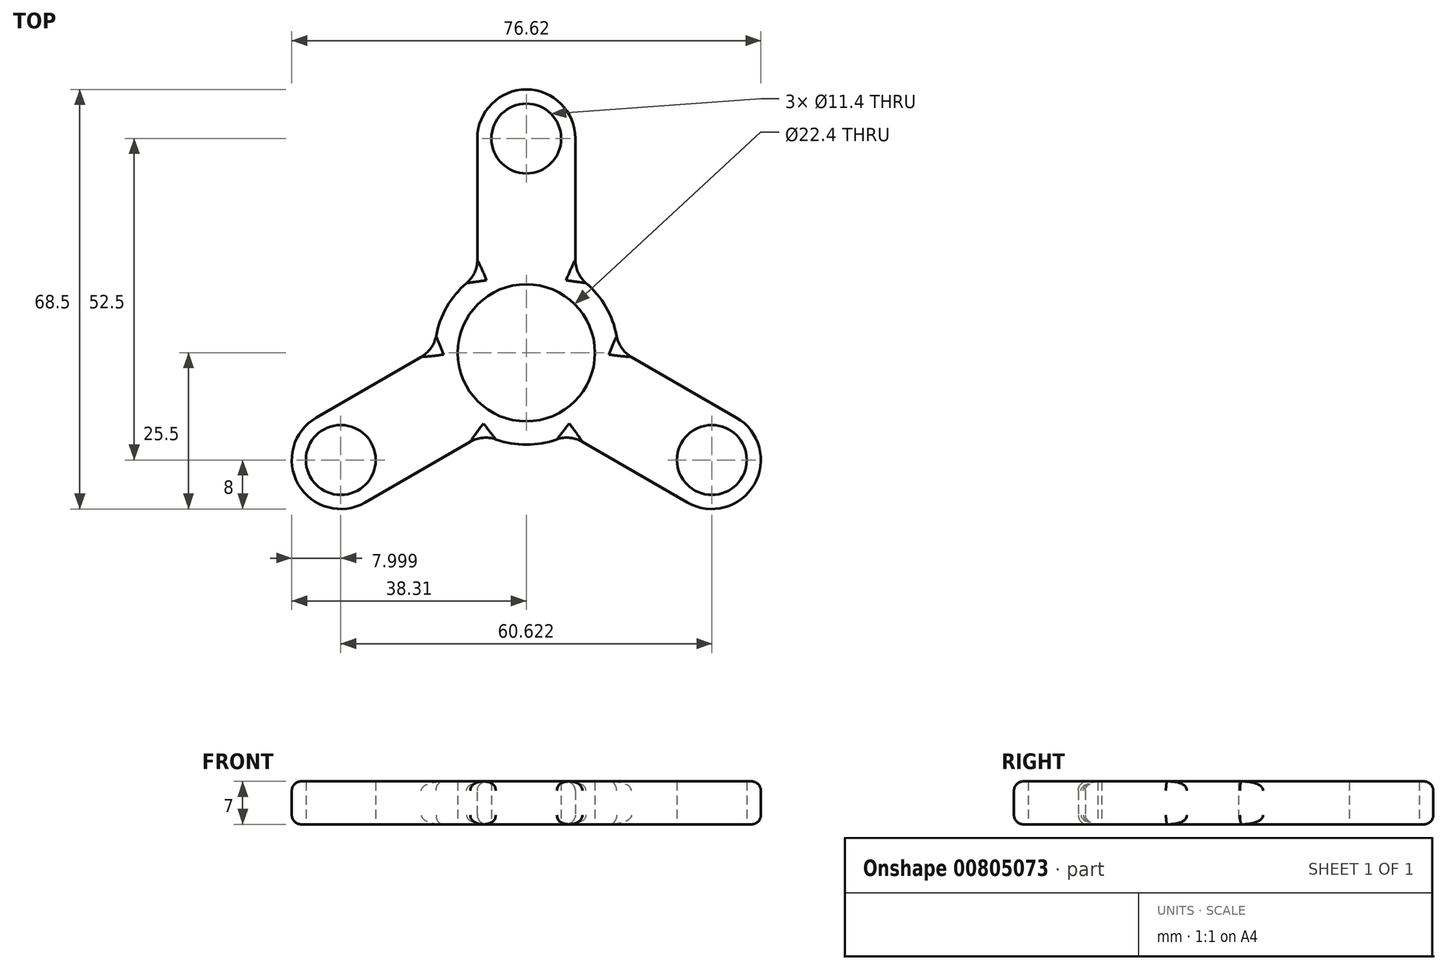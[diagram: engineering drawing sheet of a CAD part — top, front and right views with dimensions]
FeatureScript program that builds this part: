
annotation { "Feature Type Name" : "Feature", "Feature Type Description" : "" }
export const myFeature = defineFeature(function(context is Context, id is Id, definition is map)
    precondition{}
    {
        {
            var Q0;
            Q0=qCreatedBy(makeId("Top.planeOp"),FACE);
            var sketch = newSketch(context, id + "F0", { "sketchPlane" : qUnion([Q0])});
            skCircle(sketch, "E0", {"center": v(0, 0) * mm, "radius": 11.2 * mm});
            skArc(sketch, "E1", {"start": v(-8, 12.69) * mm, "mid": v(-13, 7.5) * mm, "end": v(-14.99, 0.58) * mm});
            skCircle(sketch, "E2", {"center": v(0, 35) * mm, "radius": 5.7 * mm});
            skArc(sketch, "E3", {"start": v(8, 35) * mm, "mid": v(0, 43) * mm, "end": v(-8, 35) * mm});
            skLineSegment(sketch, "E4", {"start": v(8, 35) * mm, "end": v(8, 12.69) * mm});
            skLineSegment(sketch, "E5", {"start": v(-8, 35) * mm, "end": v(-8, 12.69) * mm});
            skLineSegment(sketch, "E6.1.0", {"start": v(-34.31, -10.57) * mm, "end": v(-14.99, 0.58) * mm});
            skArc(sketch, "E6.1.1", {"start": v(-34.31, -10.57) * mm, "mid": v(-37.24, -21.5) * mm, "end": v(-26.31, -24.43) * mm});
            skCircle(sketch, "E6.1.2", {"center": v(-30.31, -17.5) * mm, "radius": 5.7 * mm});
            skLineSegment(sketch, "E6.1.3", {"start": v(-26.31, -24.43) * mm, "end": v(-6.99, -13.27) * mm});
            skLineSegment(sketch, "E6.2.0", {"start": v(26.31, -24.43) * mm, "end": v(6.99, -13.27) * mm});
            skArc(sketch, "E6.2.1", {"start": v(26.31, -24.43) * mm, "mid": v(37.24, -21.5) * mm, "end": v(34.31, -10.57) * mm});
            skCircle(sketch, "E6.2.2", {"center": v(30.31, -17.5) * mm, "radius": 5.7 * mm});
            skLineSegment(sketch, "E6.2.3", {"start": v(34.31, -10.57) * mm, "end": v(14.99, 0.58) * mm});
            skArc(sketch, "E7.trimOffspring", {"start": v(-6.99, -13.27) * mm, "mid": v(0, -15) * mm, "end": v(6.99, -13.27) * mm});
            skArc(sketch, "E8.trimOffspring", {"start": v(14.99, 0.58) * mm, "mid": v(13, 7.5) * mm, "end": v(8, 12.69) * mm});
            skSolve(sketch);
        }
        {
            var Q0;
            Q0=makeQuery(id+"F0.imprint","IMPRINT",FACE,{"disambiguationData":[TD([[makeQuery(id+"F0.imprint","IMPRINT",EDGE,{"derivedFrom":sQuery(id+"F0.wireOp",EDGE,"E0")}),-1.0]])]});
            extrude(context, id + "F1", {"entities" : qUnion([Q0]), "depth" : 7 * mm, "offsetDistance" : 25 * mm});
        }
        {
            var Q0;
            Q0=makeQuery(id+"F1.opExtrude","CAP_EDGE",EDGE,{"disambiguationData":[OSD([sQuery(id+"F0.wireOp",EDGE,"E5")])],"isStart":false});
            var Q1;
            Q1=makeQuery(id+"F1.opExtrude","CAP_EDGE",EDGE,{"disambiguationData":[OSD([sQuery(id+"F0.wireOp",EDGE,"E1")])],"isStart":false});
            var Q2;
            Q2=makeQuery(id+"F1.opExtrude","CAP_EDGE",EDGE,{"disambiguationData":[OSD([sQuery(id+"F0.wireOp",EDGE,"E6.1.0")])],"isStart":false});
            var Q3;
            Q3=makeQuery(id+"F1.opExtrude","CAP_EDGE",EDGE,{"disambiguationData":[OSD([sQuery(id+"F0.wireOp",EDGE,"E7.trimOffspring")])],"isStart":false});
            var Q4;
            Q4=makeQuery(id+"F1.opExtrude","CAP_EDGE",EDGE,{"disambiguationData":[OSD([sQuery(id+"F0.wireOp",EDGE,"E6.2.0")])],"isStart":false});
            var Q5;
            Q5=makeQuery(id+"F1.opExtrude","CAP_EDGE",EDGE,{"disambiguationData":[OSD([sQuery(id+"F0.wireOp",EDGE,"E8.trimOffspring")])],"isStart":false});
            var Q6;
            Q6=makeQuery(id+"F1.opExtrude","CAP_EDGE",EDGE,{"disambiguationData":[OSD([sQuery(id+"F0.wireOp",EDGE,"E4")])],"isStart":true});
            var Q7;
            Q7=makeQuery(id+"F1.opExtrude","CAP_EDGE",EDGE,{"disambiguationData":[OSD([sQuery(id+"F0.wireOp",EDGE,"E8.trimOffspring")])],"isStart":true});
            var Q8;
            Q8=makeQuery(id+"F1.opExtrude","CAP_EDGE",EDGE,{"disambiguationData":[OSD([sQuery(id+"F0.wireOp",EDGE,"E6.2.3")])],"isStart":true});
            var Q9;
            Q9=makeQuery(id+"F1.opExtrude","CAP_EDGE",EDGE,{"disambiguationData":[OSD([sQuery(id+"F0.wireOp",EDGE,"E7.trimOffspring")])],"isStart":true});
            var Q10;
            Q10=makeQuery(id+"F1.opExtrude","CAP_EDGE",EDGE,{"disambiguationData":[OSD([sQuery(id+"F0.wireOp",EDGE,"E6.1.3")])],"isStart":true});
            var Q11;
            Q11=makeQuery(id+"F1.opExtrude","CAP_EDGE",EDGE,{"disambiguationData":[OSD([sQuery(id+"F0.wireOp",EDGE,"E1")])],"isStart":true});
            fillet(context, id + "F2", {"entities" : qUnion([Q0, Q1, Q2, Q3, Q4, Q5, Q6, Q7, Q8, Q9, Q10, Q11]), "radius" : 1.5 * mm, "tangentPropagation" : true, "allowEdgeOverflow" : false});
        }
        {
            var Q0;
            Q0=makeQuery(id+"F1.opExtrude","SWEPT_EDGE",EDGE,{"disambiguationData":[OSD([sQuery(id+"F0.wireOp",EDGE,"E1"),sQuery(id+"F0.wireOp",EDGE,"E5")])]});
            var Q1;
            Q1=makeQuery(id+"F1.opExtrude","SWEPT_EDGE",EDGE,{"disambiguationData":[OSD([sQuery(id+"F0.wireOp",EDGE,"E1"),sQuery(id+"F0.wireOp",EDGE,"E6.1.0")])]});
            var Q2;
            Q2=makeQuery(id+"F1.opExtrude","SWEPT_EDGE",EDGE,{"disambiguationData":[OSD([sQuery(id+"F0.wireOp",EDGE,"E6.1.3"),sQuery(id+"F0.wireOp",EDGE,"E7.trimOffspring")])]});
            var Q3;
            Q3=makeQuery(id+"F1.opExtrude","SWEPT_EDGE",EDGE,{"disambiguationData":[OSD([sQuery(id+"F0.wireOp",EDGE,"E6.2.0"),sQuery(id+"F0.wireOp",EDGE,"E7.trimOffspring")])]});
            var Q4;
            Q4=makeQuery(id+"F1.opExtrude","SWEPT_EDGE",EDGE,{"disambiguationData":[OSD([sQuery(id+"F0.wireOp",EDGE,"E6.2.3"),sQuery(id+"F0.wireOp",EDGE,"E8.trimOffspring")])]});
            var Q5;
            Q5=makeQuery(id+"F1.opExtrude","SWEPT_EDGE",EDGE,{"disambiguationData":[OSD([sQuery(id+"F0.wireOp",EDGE,"E4"),sQuery(id+"F0.wireOp",EDGE,"E8.trimOffspring")])]});
            fillet(context, id + "F3", {"entities" : qUnion([Q0, Q1, Q2, Q3, Q4, Q5]), "radius" : 5 * mm, "tangentPropagation" : true, "allowEdgeOverflow" : false});
        }
    });
